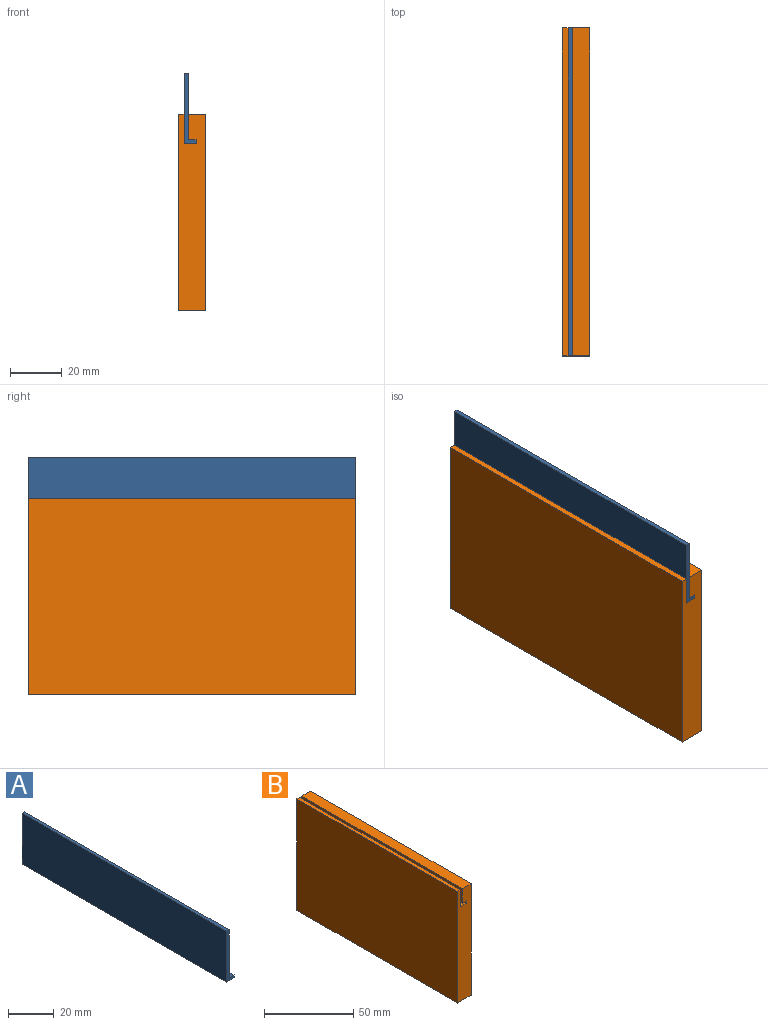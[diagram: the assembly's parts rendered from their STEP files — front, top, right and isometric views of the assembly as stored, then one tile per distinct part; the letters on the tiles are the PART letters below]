
ASSEMBLY  parts=2 mates=1
PART A: 8 faces, bbox 4.6x127x27.3 mm
  f0: plane 127x27.31mm, normal (-1,0,0), area 3467.7mm2, adj f1,f5,f6,f7
  f1: plane 127x4.65mm, normal (0,0,-1), area 590.3mm2, adj f0,f2,f6,f7
  f2: plane 127x1.57mm, normal (1,0,0), area 200mm2, adj f1,f3,f6,f7
  f3: plane 127x3.07mm, normal (0,0,1), area 390.3mm2, adj f2,f4,f6,f7
  f4: plane 127x25.73mm, normal (1,0,0), area 3267.7mm2, adj f3,f5,f6,f7
  f5: plane 127x1.57mm, normal (0,0,1), area 200mm2, adj f0,f4,f6,f7
  f6: plane 27.31x4.65mm, normal (0,-1,0), area 47.8mm2, adj f0,f1,f2,f3,f4,f5
  f7: plane 27.31x4.65mm, normal (0,1,0), area 47.8mm2, adj f0,f1,f2,f3,f4,f5
PART B: 12 faces, bbox 10.8x127x76.2 mm
  f0: plane 127x11.43mm, normal (1,0,0), area 1451.6mm2, adj f1,f9,f10,f11
  f1: plane 127x2.29mm, normal (0,0,1), area 290.3mm2, adj f0,f2,f10,f11
  f2: plane 127x76.2mm, normal (-1,0,0), area 9677.4mm2, adj f1,f3,f10,f11
  f3: plane 127x10.77mm, normal (0,0,-1), area 1367.7mm2, adj f2,f4,f10,f11
  f4: plane 127x76.2mm, normal (1,0,0), area 9677.4mm2, adj f3,f5,f10,f11
  f5: plane 127x6.88mm, normal (0,0,1), area 874.2mm2, adj f4,f6,f10,f11
  f6: plane 127x9.83mm, normal (-1,0,0), area 1248.4mm2, adj f5,f7,f10,f11
  f7: plane 127x3.07mm, normal (0,0,-1), area 390.3mm2, adj f6,f8,f10,f11
  f8: plane 127x1.6mm, normal (-1,0,0), area 203.2mm2, adj f7,f9,f10,f11
  f9: plane 127x4.67mm, normal (0,0,1), area 593.5mm2, adj f0,f8,f10,f11
  f10: plane 76.2x10.77mm, normal (0,-1,0), area 797.4mm2, adj f0,f1,f2,f3,f4,f5,f6,f7
  f11: plane 76.2x10.77mm, normal (0,1,0), area 797.4mm2, adj f0,f1,f2,f3,f4,f5,f6,f7
PLACE A t=(-43.71,11.3,-19.12)mm
PLACE B t=(-43.73,11.3,-19.12)mm fixed
MATE fastened A.f1 <-> B.f9  axis (0,0,-1) through (-41.39,-52.2,-19.12)mm
